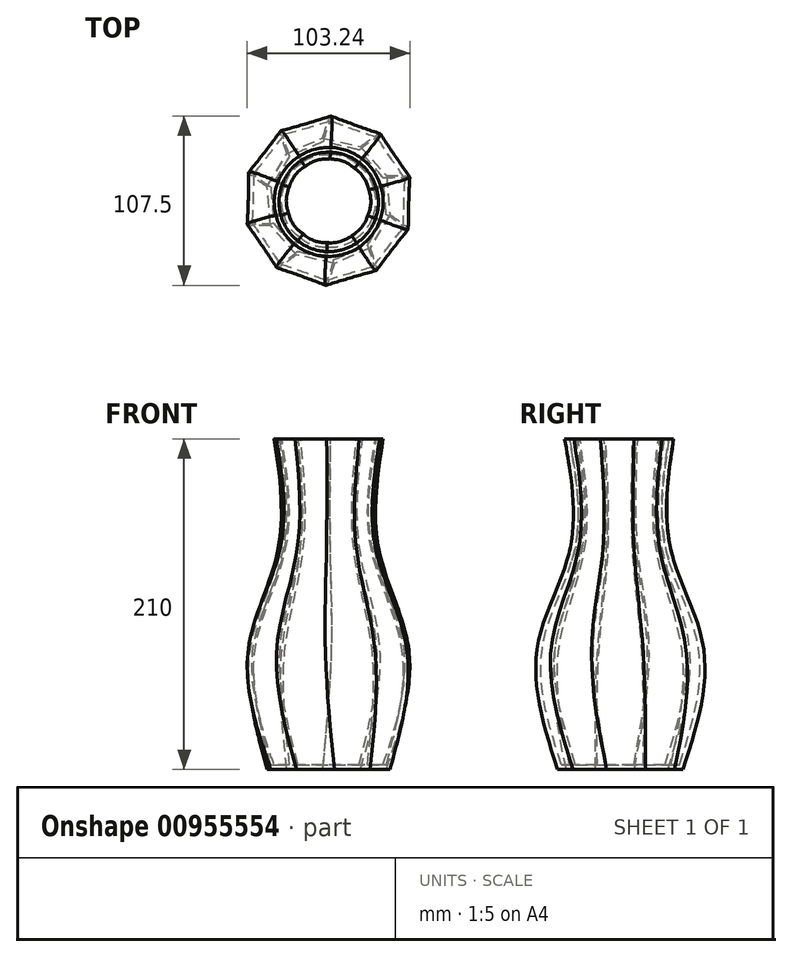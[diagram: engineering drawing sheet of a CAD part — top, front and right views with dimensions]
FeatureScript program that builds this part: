
annotation { "Feature Type Name" : "Feature", "Feature Type Description" : "" }
export const myFeature = defineFeature(function(context is Context, id is Id, definition is map)
    precondition{}
    {
        {
            var Q0;
            Q0=qCreatedBy(makeId("Top.planeOp"),FACE);
            var sketch = newSketch(context, id + "F0", { "sketchPlane" : qUnion([Q0])});
            skCircle(sketch, "E0.cCircle", {"center": v(0, 0) * mm, "radius": 40 * mm, "construction": true});
            skLineSegment(sketch, "E0.0", {"start": v(-3.68, 39.83) * mm, "end": v(20.43, 34.39) * mm});
            skLineSegment(sketch, "E0.1", {"start": v(20.43, 34.39) * mm, "end": v(36.74, 15.8) * mm});
            skLineSegment(sketch, "E0.2", {"start": v(36.74, 15.8) * mm, "end": v(39.02, -8.8) * mm});
            skLineSegment(sketch, "E0.3", {"start": v(39.02, -8.8) * mm, "end": v(26.39, -30.06) * mm});
            skLineSegment(sketch, "E0.4", {"start": v(26.39, -30.06) * mm, "end": v(3.68, -39.83) * mm});
            skLineSegment(sketch, "E0.5", {"start": v(3.68, -39.83) * mm, "end": v(-20.43, -34.39) * mm});
            skLineSegment(sketch, "E0.6", {"start": v(-20.43, -34.39) * mm, "end": v(-36.74, -15.8) * mm});
            skLineSegment(sketch, "E0.7", {"start": v(-36.74, -15.8) * mm, "end": v(-39.02, 8.8) * mm});
            skLineSegment(sketch, "E0.8", {"start": v(-39.02, 8.8) * mm, "end": v(-26.39, 30.06) * mm});
            skLineSegment(sketch, "E0.9", {"start": v(-26.39, 30.06) * mm, "end": v(-3.68, 39.83) * mm});
            skSolve(sketch);
        }
        {
            var Q0;
            Q0=qCreatedBy(makeId("Top.planeOp"),FACE);
            cPlane(context, id + "F1", {"entities" : qUnion([Q0]), "cplaneType" : CPlaneType.OFFSET, "offset" : 80 * mm, "width" : 150 * mm, "height" : 150 * mm});
        }
        {
            var Q0;
            Q0=qCreatedBy(id+"F1.planeOp",FACE);
            var sketch = newSketch(context, id + "F2", { "sketchPlane" : qUnion([Q0])});
            skCircle(sketch, "E1.cCircle", {"center": v(0, 0) * mm, "radius": 52.37 * mm, "construction": true});
            skLineSegment(sketch, "E1.0", {"start": v(50.43, 14.13) * mm, "end": v(49.1, -18.21) * mm});
            skLineSegment(sketch, "E1.1", {"start": v(49.1, -18.21) * mm, "end": v(29.02, -43.6) * mm});
            skLineSegment(sketch, "E1.2", {"start": v(29.02, -43.6) * mm, "end": v(-2.15, -52.33) * mm});
            skLineSegment(sketch, "E1.3", {"start": v(-2.15, -52.33) * mm, "end": v(-32.5, -41.07) * mm});
            skLineSegment(sketch, "E1.4", {"start": v(-32.5, -41.07) * mm, "end": v(-50.43, -14.13) * mm});
            skLineSegment(sketch, "E1.5", {"start": v(-50.43, -14.13) * mm, "end": v(-49.1, 18.21) * mm});
            skLineSegment(sketch, "E1.6", {"start": v(-49.1, 18.21) * mm, "end": v(-29.02, 43.6) * mm});
            skLineSegment(sketch, "E1.7", {"start": v(-29.02, 43.6) * mm, "end": v(2.15, 52.33) * mm});
            skLineSegment(sketch, "E1.8", {"start": v(2.15, 52.33) * mm, "end": v(32.5, 41.07) * mm});
            skLineSegment(sketch, "E1.9", {"start": v(32.5, 41.07) * mm, "end": v(50.43, 14.13) * mm});
            skSolve(sketch);
        }
        {
            var Q0;
            Q0=qCreatedBy(id+"F1.planeOp",FACE);
            cPlane(context, id + "F3", {"entities" : qUnion([Q0]), "cplaneType" : CPlaneType.OFFSET, "offset" : 60 * mm, "width" : 150 * mm, "height" : 150 * mm});
        }
        {
            var Q0;
            Q0=qCreatedBy(id+"F3.planeOp",FACE);
            var sketch = newSketch(context, id + "F4", { "sketchPlane" : qUnion([Q0])});
            skCircle(sketch, "E2", {"center": v(0, 0) * mm, "radius": 32 * mm});
            skSolve(sketch);
        }
        {
            var Q0;
            Q0=qCreatedBy(id+"F3.planeOp",FACE);
            cPlane(context, id + "F5", {"entities" : qUnion([Q0]), "cplaneType" : CPlaneType.OFFSET, "offset" : 70 * mm, "width" : 150 * mm, "height" : 150 * mm});
        }
        {
            var Q0;
            Q0=qCreatedBy(id+"F5.planeOp",FACE);
            var sketch = newSketch(context, id + "F6", { "sketchPlane" : qUnion([Q0])});
            skCircle(sketch, "E3", {"center": v(0.14, -0.79) * mm, "radius": 34.6 * mm});
            skSolve(sketch);
        }
        {
            var Q0;
            Q0=makeQuery(id+"F0.imprint","IMPRINT",FACE,{"disambiguationData":[TD([[makeQuery(id+"F0.imprint","IMPRINT",EDGE,{"derivedFrom":sQuery(id+"F0.wireOp",EDGE,"E0.0")}),-1.0]])]});
            var Q1;
            Q1=makeQuery(id+"F2.imprint","IMPRINT",FACE,{"disambiguationData":[TD([[makeQuery(id+"F2.imprint","IMPRINT",EDGE,{"derivedFrom":sQuery(id+"F2.wireOp",EDGE,"E1.0")}),-1.0]])]});
            var Q2;
            Q2=makeQuery(id+"F4.imprint","IMPRINT",FACE,{"disambiguationData":[TD([[makeQuery(id+"F4.imprint","IMPRINT",EDGE,{"derivedFrom":sQuery(id+"F4.wireOp",EDGE,"E2")}),1.0]])]});
            var Q3;
            Q3=makeQuery(id+"F6.imprint","IMPRINT",FACE,{"disambiguationData":[TD([[makeQuery(id+"F6.imprint","IMPRINT",EDGE,{"derivedFrom":sQuery(id+"F6.wireOp",EDGE,"E3")}),1.0]])]});
            loft(context, id + "F7", {"sheetProfilesArray" : [{ "sheetProfileEntities" : qUnion([Q0]) }, { "sheetProfileEntities" : qUnion([Q1]) }, { "sheetProfileEntities" : qUnion([Q2]) }, { "sheetProfileEntities" : qUnion([Q3]) }]});
        }
        {
            var Q0;
            Q0=makeQuery(id+"F7.opLoft","CAP_FACE",FACE,{"disambiguationData":[OSD([makeQuery(id+"F6.imprint","IMPRINT",FACE,{"disambiguationData":[TD([[makeQuery(id+"F6.imprint","IMPRINT",EDGE,{"derivedFrom":sQuery(id+"F6.wireOp",EDGE,"E3")}),1.0]])]})])],"isStart":true});
            shell(context, id + "F8", {"entities" : qUnion([Q0]), "thickness" : 3 * mm});
        }
    });
